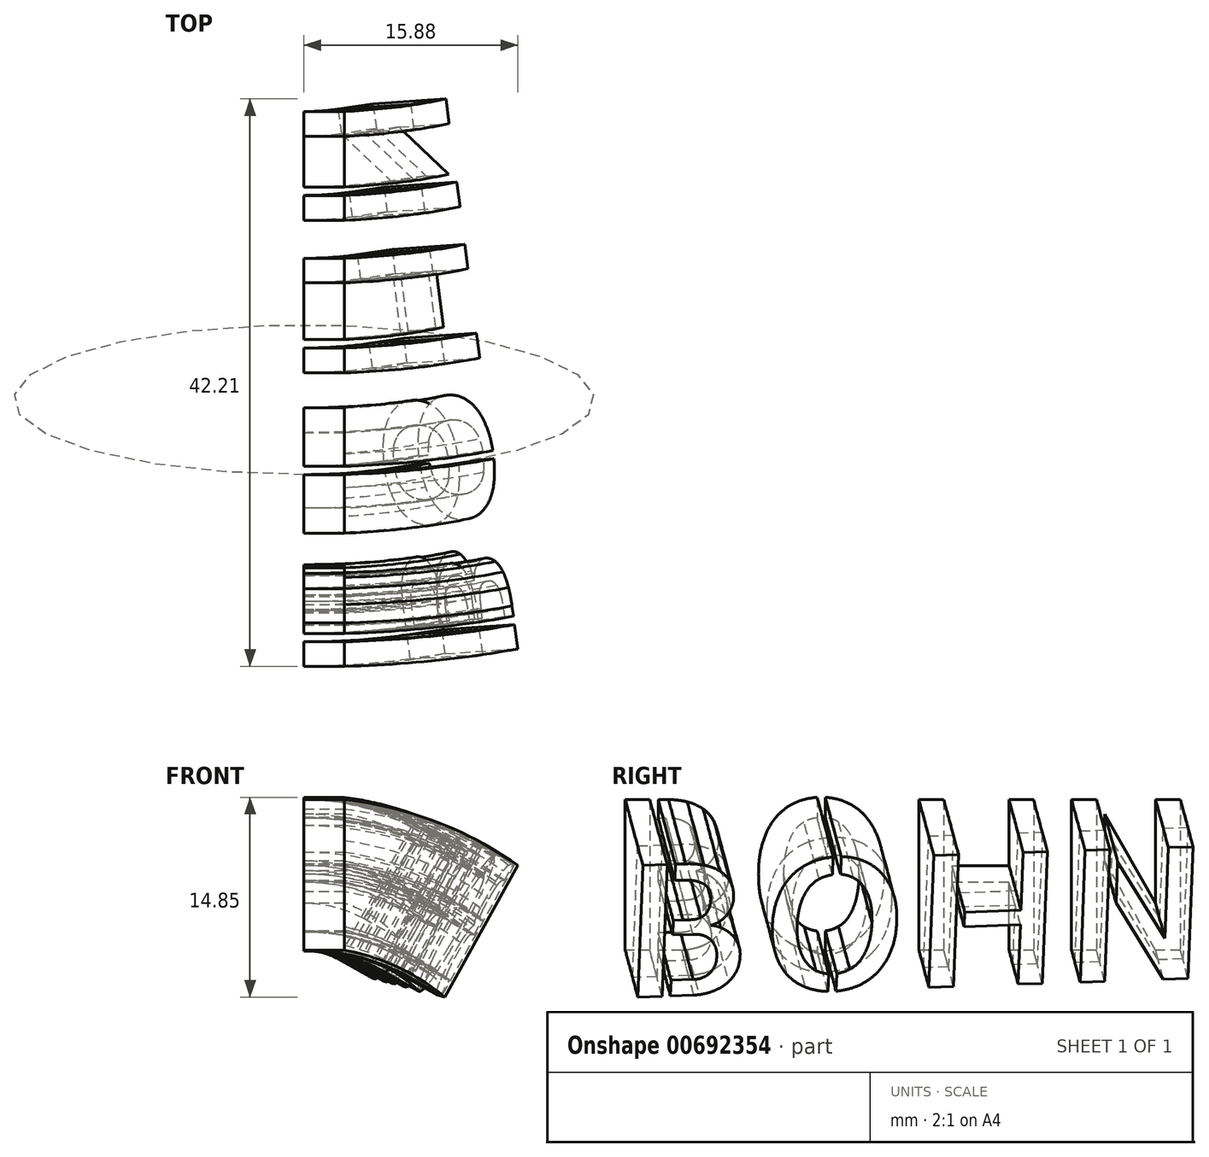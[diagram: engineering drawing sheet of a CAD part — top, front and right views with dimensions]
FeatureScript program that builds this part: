
annotation { "Feature Type Name" : "Feature", "Feature Type Description" : "" }
export const myFeature = defineFeature(function(context is Context, id is Id, definition is map)
    precondition{}
    {
        {
            var Q0;
            Q0=qCreatedBy(makeId("Right.planeOp"),FACE);
            var sketch = newSketch(context, id + "F0", { "sketchPlane" : qUnion([Q0])});
            skText(sketch, "E0", { "text": "BOHN", "fontName": "AllertaStencil-Regular.ttf"});
            const initialGuessF0  = {"E0": [-0.01671, 0.0177, 1, 0, 0.0112]};
            skSetInitialGuess(sketch, initialGuessF0);
            skSolve(sketch);
        }
        {
            var Q0;
            Q0=makeQuery(id+"F0.imprint","IMPRINT",FACE,{"disambiguationData":[TD([[makeQuery(id+"F0.imprint","IMPRINT",EDGE,{"derivedFrom":sQuery(id+"F0.wireOp",EDGE,"E0.sketch_text.stroke-79")}),-1.0]])]});
            var sketch = newSketch(context, id + "F1", { "sketchPlane" : qUnion([Q0])});
            skPoint(sketch, "E1", {"position": v(-30.52, 17.7) * mm});
            skPoint(sketch, "E2", {"position": v(-30.52, 31.5) * mm});
            skPoint(sketch, "E3", {"position": v(-22.23, 5.05) * mm});
            skSolve(sketch);
        }
        {
            var Q0;
            Q0 = qSketchRegion(id + "F0", true);
            extrude(context, id + "F2", {"entities" : qUnion([Q0]), "depth" : 3 * mm, "offsetDistance" : 25 * mm});
        }
        {
            var Q0;
            Q0=qCreatedBy(makeId("Right.planeOp"),FACE);
            var sketch = newSketch(context, id + "F3", { "sketchPlane" : qUnion([Q0])});
            skLineSegment(sketch, "E4", {"start": v(-30.76, -2.74) * mm, "end": v(47.8, 18.27) * mm, "construction": true});
            skSolve(sketch);
        }
        {
            var Q0;
            Q0=makeQuery(id+"F2.opExtrude","SWEPT_FACE",FACE,{"disambiguationData":[OSD([sQuery(id+"F0.wireOp",EDGE,"E0.sketch_text.stroke-17")])]});
            var Q1;
            Q1=makeQuery(id+"F2.opExtrude","SWEPT_FACE",FACE,{"disambiguationData":[OSD([sQuery(id+"F0.wireOp",EDGE,"E0.sketch_text.stroke-28")])]});
            var Q2;
            Q2=makeQuery(id+"F2.opExtrude","SWEPT_FACE",FACE,{"disambiguationData":[OSD([sQuery(id+"F0.wireOp",EDGE,"E0.sketch_text.stroke-29")])]});
            var Q3;
            Q3=makeQuery(id+"F2.opExtrude","SWEPT_FACE",FACE,{"disambiguationData":[OSD([sQuery(id+"F0.wireOp",EDGE,"E0.sketch_text.stroke-10")])]});
            var Q4;
            Q4=makeQuery(id+"F2.opExtrude","CAP_FACE",FACE,{"disambiguationData":[OSD([sQuery(id+"F0.wireOp",EDGE,"E0.sketch_text.stroke-0"),sQuery(id+"F0.wireOp",EDGE,"E0.sketch_text.stroke-1"),sQuery(id+"F0.wireOp",EDGE,"E0.sketch_text.stroke-2"),sQuery(id+"F0.wireOp",EDGE,"E0.sketch_text.stroke-3"),sQuery(id+"F0.wireOp",EDGE,"E0.sketch_text.stroke-4"),sQuery(id+"F0.wireOp",EDGE,"E0.sketch_text.stroke-5"),sQuery(id+"F0.wireOp",EDGE,"E0.sketch_text.stroke-6"),sQuery(id+"F0.wireOp",EDGE,"E0.sketch_text.stroke-7"),sQuery(id+"F0.wireOp",EDGE,"E0.sketch_text.stroke-8"),sQuery(id+"F0.wireOp",EDGE,"E0.sketch_text.stroke-9"),sQuery(id+"F0.wireOp",EDGE,"E0.sketch_text.stroke-10"),sQuery(id+"F0.wireOp",EDGE,"E0.sketch_text.stroke-11"),sQuery(id+"F0.wireOp",EDGE,"E0.sketch_text.stroke-12"),sQuery(id+"F0.wireOp",EDGE,"E0.sketch_text.stroke-13"),sQuery(id+"F0.wireOp",EDGE,"E0.sketch_text.stroke-14"),sQuery(id+"F0.wireOp",EDGE,"E0.sketch_text.stroke-15"),sQuery(id+"F0.wireOp",EDGE,"E0.sketch_text.stroke-16"),sQuery(id+"F0.wireOp",EDGE,"E0.sketch_text.stroke-17"),sQuery(id+"F0.wireOp",EDGE,"E0.sketch_text.stroke-18"),sQuery(id+"F0.wireOp",EDGE,"E0.sketch_text.stroke-19"),sQuery(id+"F0.wireOp",EDGE,"E0.sketch_text.stroke-20"),sQuery(id+"F0.wireOp",EDGE,"E0.sketch_text.stroke-21"),sQuery(id+"F0.wireOp",EDGE,"E0.sketch_text.stroke-22"),sQuery(id+"F0.wireOp",EDGE,"E0.sketch_text.stroke-23"),sQuery(id+"F0.wireOp",EDGE,"E0.sketch_text.stroke-24"),sQuery(id+"F0.wireOp",EDGE,"E0.sketch_text.stroke-25"),sQuery(id+"F0.wireOp",EDGE,"E0.sketch_text.stroke-26"),sQuery(id+"F0.wireOp",EDGE,"E0.sketch_text.stroke-27"),sQuery(id+"F0.wireOp",EDGE,"E0.sketch_text.stroke-28"),sQuery(id+"F0.wireOp",EDGE,"E0.sketch_text.stroke-29"),sQuery(id+"F0.wireOp",EDGE,"E0.sketch_text.stroke-30"),sQuery(id+"F0.wireOp",EDGE,"E0.sketch_text.stroke-31"),sQuery(id+"F0.wireOp",EDGE,"E0.sketch_text.stroke-32"),sQuery(id+"F0.wireOp",EDGE,"E0.sketch_text.stroke-33"),sQuery(id+"F0.wireOp",EDGE,"E0.sketch_text.stroke-34"),sQuery(id+"F0.wireOp",EDGE,"E0.sketch_text.stroke-35"),sQuery(id+"F0.wireOp",EDGE,"E0.sketch_text.stroke-36"),sQuery(id+"F0.wireOp",EDGE,"E0.sketch_text.stroke-37"),sQuery(id+"F0.wireOp",EDGE,"E0.sketch_text.stroke-38")])],"isStart":false});
            var Q5;
            Q5=makeQuery(id+"F2.opExtrude","SWEPT_FACE",FACE,{"disambiguationData":[OSD([sQuery(id+"F0.wireOp",EDGE,"E0.sketch_text.stroke-12")])]});
            var Q6;
            Q6=makeQuery(id+"F2.opExtrude","SWEPT_FACE",FACE,{"disambiguationData":[OSD([sQuery(id+"F0.wireOp",EDGE,"E0.sketch_text.stroke-11")])]});
            var Q7;
            Q7=makeQuery(id+"F2.opExtrude","SWEPT_FACE",FACE,{"disambiguationData":[OSD([sQuery(id+"F0.wireOp",EDGE,"E0.sketch_text.stroke-41")])]});
            var Q8;
            Q8=makeQuery(id+"F2.opExtrude","SWEPT_FACE",FACE,{"disambiguationData":[OSD([sQuery(id+"F0.wireOp",EDGE,"E0.sketch_text.stroke-42")])]});
            var Q9;
            Q9=makeQuery(id+"F2.opExtrude","SWEPT_FACE",FACE,{"disambiguationData":[OSD([sQuery(id+"F0.wireOp",EDGE,"E0.sketch_text.stroke-39")])]});
            var Q10;
            Q10=makeQuery(id+"F2.opExtrude","CAP_FACE",FACE,{"disambiguationData":[OSD([sQuery(id+"F0.wireOp",EDGE,"E0.sketch_text.stroke-39"),sQuery(id+"F0.wireOp",EDGE,"E0.sketch_text.stroke-40"),sQuery(id+"F0.wireOp",EDGE,"E0.sketch_text.stroke-41"),sQuery(id+"F0.wireOp",EDGE,"E0.sketch_text.stroke-42")])],"isStart":false});
            var Q11;
            Q11=makeQuery(id+"F2.opExtrude","SWEPT_FACE",FACE,{"disambiguationData":[OSD([sQuery(id+"F0.wireOp",EDGE,"E0.sketch_text.stroke-56")])]});
            var Q12;
            Q12=makeQuery(id+"F2.opExtrude","CAP_FACE",FACE,{"disambiguationData":[OSD([sQuery(id+"F0.wireOp",EDGE,"E0.sketch_text.stroke-43"),sQuery(id+"F0.wireOp",EDGE,"E0.sketch_text.stroke-44"),sQuery(id+"F0.wireOp",EDGE,"E0.sketch_text.stroke-45"),sQuery(id+"F0.wireOp",EDGE,"E0.sketch_text.stroke-46"),sQuery(id+"F0.wireOp",EDGE,"E0.sketch_text.stroke-47"),sQuery(id+"F0.wireOp",EDGE,"E0.sketch_text.stroke-48"),sQuery(id+"F0.wireOp",EDGE,"E0.sketch_text.stroke-49"),sQuery(id+"F0.wireOp",EDGE,"E0.sketch_text.stroke-50"),sQuery(id+"F0.wireOp",EDGE,"E0.sketch_text.stroke-51"),sQuery(id+"F0.wireOp",EDGE,"E0.sketch_text.stroke-52"),sQuery(id+"F0.wireOp",EDGE,"E0.sketch_text.stroke-53"),sQuery(id+"F0.wireOp",EDGE,"E0.sketch_text.stroke-54"),sQuery(id+"F0.wireOp",EDGE,"E0.sketch_text.stroke-55"),sQuery(id+"F0.wireOp",EDGE,"E0.sketch_text.stroke-56"),sQuery(id+"F0.wireOp",EDGE,"E0.sketch_text.stroke-57"),sQuery(id+"F0.wireOp",EDGE,"E0.sketch_text.stroke-58"),sQuery(id+"F0.wireOp",EDGE,"E0.sketch_text.stroke-59"),sQuery(id+"F0.wireOp",EDGE,"E0.sketch_text.stroke-60")])],"isStart":false});
            var Q13;
            Q13=makeQuery(id+"F2.opExtrude","SWEPT_FACE",FACE,{"disambiguationData":[OSD([sQuery(id+"F0.wireOp",EDGE,"E0.sketch_text.stroke-69")])]});
            var Q14;
            Q14=makeQuery(id+"F2.opExtrude","CAP_FACE",FACE,{"disambiguationData":[OSD([sQuery(id+"F0.wireOp",EDGE,"E0.sketch_text.stroke-61"),sQuery(id+"F0.wireOp",EDGE,"E0.sketch_text.stroke-62"),sQuery(id+"F0.wireOp",EDGE,"E0.sketch_text.stroke-63"),sQuery(id+"F0.wireOp",EDGE,"E0.sketch_text.stroke-64"),sQuery(id+"F0.wireOp",EDGE,"E0.sketch_text.stroke-65"),sQuery(id+"F0.wireOp",EDGE,"E0.sketch_text.stroke-66"),sQuery(id+"F0.wireOp",EDGE,"E0.sketch_text.stroke-67"),sQuery(id+"F0.wireOp",EDGE,"E0.sketch_text.stroke-68"),sQuery(id+"F0.wireOp",EDGE,"E0.sketch_text.stroke-69"),sQuery(id+"F0.wireOp",EDGE,"E0.sketch_text.stroke-70"),sQuery(id+"F0.wireOp",EDGE,"E0.sketch_text.stroke-71"),sQuery(id+"F0.wireOp",EDGE,"E0.sketch_text.stroke-72"),sQuery(id+"F0.wireOp",EDGE,"E0.sketch_text.stroke-73"),sQuery(id+"F0.wireOp",EDGE,"E0.sketch_text.stroke-74"),sQuery(id+"F0.wireOp",EDGE,"E0.sketch_text.stroke-75"),sQuery(id+"F0.wireOp",EDGE,"E0.sketch_text.stroke-76"),sQuery(id+"F0.wireOp",EDGE,"E0.sketch_text.stroke-77"),sQuery(id+"F0.wireOp",EDGE,"E0.sketch_text.stroke-78")])],"isStart":false});
            var Q15;
            Q15=makeQuery(id+"F2.opExtrude","SWEPT_FACE",FACE,{"disambiguationData":[OSD([sQuery(id+"F0.wireOp",EDGE,"E0.sketch_text.stroke-78")])]});
            var Q16;
            Q16=makeQuery(id+"F2.opExtrude","SWEPT_FACE",FACE,{"disambiguationData":[OSD([sQuery(id+"F0.wireOp",EDGE,"E0.sketch_text.stroke-85")])]});
            var Q17;
            Q17=makeQuery(id+"F2.opExtrude","SWEPT_FACE",FACE,{"disambiguationData":[OSD([sQuery(id+"F0.wireOp",EDGE,"E0.sketch_text.stroke-83")])]});
            var Q18;
            Q18=makeQuery(id+"F2.opExtrude","SWEPT_FACE",FACE,{"disambiguationData":[OSD([sQuery(id+"F0.wireOp",EDGE,"E0.sketch_text.stroke-84")])]});
            var Q19;
            Q19=makeQuery(id+"F2.opExtrude","SWEPT_FACE",FACE,{"disambiguationData":[OSD([sQuery(id+"F0.wireOp",EDGE,"E0.sketch_text.stroke-86")])]});
            var Q20;
            Q20=makeQuery(id+"F2.opExtrude","SWEPT_FACE",FACE,{"disambiguationData":[OSD([sQuery(id+"F0.wireOp",EDGE,"E0.sketch_text.stroke-79")])]});
            var Q21;
            Q21=makeQuery(id+"F2.opExtrude","CAP_FACE",FACE,{"disambiguationData":[OSD([sQuery(id+"F0.wireOp",EDGE,"E0.sketch_text.stroke-79"),sQuery(id+"F0.wireOp",EDGE,"E0.sketch_text.stroke-80"),sQuery(id+"F0.wireOp",EDGE,"E0.sketch_text.stroke-81"),sQuery(id+"F0.wireOp",EDGE,"E0.sketch_text.stroke-82"),sQuery(id+"F0.wireOp",EDGE,"E0.sketch_text.stroke-83"),sQuery(id+"F0.wireOp",EDGE,"E0.sketch_text.stroke-84"),sQuery(id+"F0.wireOp",EDGE,"E0.sketch_text.stroke-85"),sQuery(id+"F0.wireOp",EDGE,"E0.sketch_text.stroke-86")])],"isStart":false});
            var Q22;
            Q22=makeQuery(id+"F2.opExtrude","SWEPT_FACE",FACE,{"disambiguationData":[OSD([sQuery(id+"F0.wireOp",EDGE,"E0.sketch_text.stroke-82")])]});
            var Q23;
            Q23=makeQuery(id+"F2.opExtrude","SWEPT_FACE",FACE,{"disambiguationData":[OSD([sQuery(id+"F0.wireOp",EDGE,"E0.sketch_text.stroke-87")])]});
            var Q24;
            Q24=makeQuery(id+"F2.opExtrude","CAP_FACE",FACE,{"disambiguationData":[OSD([sQuery(id+"F0.wireOp",EDGE,"E0.sketch_text.stroke-87"),sQuery(id+"F0.wireOp",EDGE,"E0.sketch_text.stroke-88"),sQuery(id+"F0.wireOp",EDGE,"E0.sketch_text.stroke-89"),sQuery(id+"F0.wireOp",EDGE,"E0.sketch_text.stroke-90")])],"isStart":false});
            var Q25;
            Q25=makeQuery(id+"F2.opExtrude","SWEPT_FACE",FACE,{"disambiguationData":[OSD([sQuery(id+"F0.wireOp",EDGE,"E0.sketch_text.stroke-89")])]});
            var Q26;
            Q26=makeQuery(id+"F2.opExtrude","SWEPT_FACE",FACE,{"disambiguationData":[OSD([sQuery(id+"F0.wireOp",EDGE,"E0.sketch_text.stroke-90")])]});
            var Q27;
            Q27=makeQuery(id+"F2.opExtrude","SWEPT_FACE",FACE,{"disambiguationData":[OSD([sQuery(id+"F0.wireOp",EDGE,"E0.sketch_text.stroke-97")])]});
            var Q28;
            Q28=makeQuery(id+"F2.opExtrude","SWEPT_FACE",FACE,{"disambiguationData":[OSD([sQuery(id+"F0.wireOp",EDGE,"E0.sketch_text.stroke-95")])]});
            var Q29;
            Q29=makeQuery(id+"F2.opExtrude","SWEPT_FACE",FACE,{"disambiguationData":[OSD([sQuery(id+"F0.wireOp",EDGE,"E0.sketch_text.stroke-96")])]});
            var Q30;
            Q30=makeQuery(id+"F2.opExtrude","SWEPT_FACE",FACE,{"disambiguationData":[OSD([sQuery(id+"F0.wireOp",EDGE,"E0.sketch_text.stroke-91")])]});
            var Q31;
            Q31=makeQuery(id+"F2.opExtrude","CAP_FACE",FACE,{"disambiguationData":[OSD([sQuery(id+"F0.wireOp",EDGE,"E0.sketch_text.stroke-91"),sQuery(id+"F0.wireOp",EDGE,"E0.sketch_text.stroke-92"),sQuery(id+"F0.wireOp",EDGE,"E0.sketch_text.stroke-93"),sQuery(id+"F0.wireOp",EDGE,"E0.sketch_text.stroke-94"),sQuery(id+"F0.wireOp",EDGE,"E0.sketch_text.stroke-95"),sQuery(id+"F0.wireOp",EDGE,"E0.sketch_text.stroke-96"),sQuery(id+"F0.wireOp",EDGE,"E0.sketch_text.stroke-97")])],"isStart":false});
            var Q32;
            Q32=makeQuery(id+"F2.opExtrude","SWEPT_FACE",FACE,{"disambiguationData":[OSD([sQuery(id+"F0.wireOp",EDGE,"E0.sketch_text.stroke-92")])]});
            var Q33;
            Q33=makeQuery(id+"F2.opExtrude","SWEPT_FACE",FACE,{"disambiguationData":[OSD([sQuery(id+"F0.wireOp",EDGE,"E0.sketch_text.stroke-93")])]});
            var Q34;
            Q34=makeQuery(id+"F2.opExtrude","SWEPT_FACE",FACE,{"disambiguationData":[OSD([sQuery(id+"F0.wireOp",EDGE,"E0.sketch_text.stroke-98")])]});
            var Q35;
            Q35=makeQuery(id+"F2.opExtrude","CAP_FACE",FACE,{"disambiguationData":[OSD([sQuery(id+"F0.wireOp",EDGE,"E0.sketch_text.stroke-98"),sQuery(id+"F0.wireOp",EDGE,"E0.sketch_text.stroke-99"),sQuery(id+"F0.wireOp",EDGE,"E0.sketch_text.stroke-100"),sQuery(id+"F0.wireOp",EDGE,"E0.sketch_text.stroke-101")])],"isStart":false});
            var Q36;
            Q36=makeQuery(id+"F2.opExtrude","SWEPT_FACE",FACE,{"disambiguationData":[OSD([sQuery(id+"F0.wireOp",EDGE,"E0.sketch_text.stroke-100")])]});
            var Q37;
            Q37=makeQuery(id+"F1.imprint","IMPRINT",FACE,{"disambiguationData":[TD([[makeQuery(id+"F1.imprint","IMPRINT",EDGE,{"derivedFrom":makeQuery(id+"F0.imprint","IMPRINT",EDGE,{"derivedFrom":sQuery(id+"F0.wireOp",EDGE,"E0.sketch_text.stroke-79")})}),-1.0]])]});
            var Q38;
            Q38=makeQuery(id+"F2.opExtrude","SWEPT_FACE",FACE,{"disambiguationData":[OSD([sQuery(id+"F0.wireOp",EDGE,"E0.sketch_text.stroke-30")])]});
            var Q39;
            Q39=makeQuery(id+"F2.opExtrude","SWEPT_FACE",FACE,{"disambiguationData":[OSD([sQuery(id+"F0.wireOp",EDGE,"E0.sketch_text.stroke-18")])]});
            var Q40;
            Q40=makeQuery(id+"F2.opExtrude","CAP_FACE",FACE,{"disambiguationData":[OSD([sQuery(id+"F0.wireOp",EDGE,"E0.sketch_text.stroke-0"),sQuery(id+"F0.wireOp",EDGE,"E0.sketch_text.stroke-1"),sQuery(id+"F0.wireOp",EDGE,"E0.sketch_text.stroke-2"),sQuery(id+"F0.wireOp",EDGE,"E0.sketch_text.stroke-3"),sQuery(id+"F0.wireOp",EDGE,"E0.sketch_text.stroke-4"),sQuery(id+"F0.wireOp",EDGE,"E0.sketch_text.stroke-5"),sQuery(id+"F0.wireOp",EDGE,"E0.sketch_text.stroke-6"),sQuery(id+"F0.wireOp",EDGE,"E0.sketch_text.stroke-7"),sQuery(id+"F0.wireOp",EDGE,"E0.sketch_text.stroke-8"),sQuery(id+"F0.wireOp",EDGE,"E0.sketch_text.stroke-9"),sQuery(id+"F0.wireOp",EDGE,"E0.sketch_text.stroke-10"),sQuery(id+"F0.wireOp",EDGE,"E0.sketch_text.stroke-11"),sQuery(id+"F0.wireOp",EDGE,"E0.sketch_text.stroke-12"),sQuery(id+"F0.wireOp",EDGE,"E0.sketch_text.stroke-13"),sQuery(id+"F0.wireOp",EDGE,"E0.sketch_text.stroke-14"),sQuery(id+"F0.wireOp",EDGE,"E0.sketch_text.stroke-15"),sQuery(id+"F0.wireOp",EDGE,"E0.sketch_text.stroke-16"),sQuery(id+"F0.wireOp",EDGE,"E0.sketch_text.stroke-17"),sQuery(id+"F0.wireOp",EDGE,"E0.sketch_text.stroke-18"),sQuery(id+"F0.wireOp",EDGE,"E0.sketch_text.stroke-19"),sQuery(id+"F0.wireOp",EDGE,"E0.sketch_text.stroke-20"),sQuery(id+"F0.wireOp",EDGE,"E0.sketch_text.stroke-21"),sQuery(id+"F0.wireOp",EDGE,"E0.sketch_text.stroke-22"),sQuery(id+"F0.wireOp",EDGE,"E0.sketch_text.stroke-23"),sQuery(id+"F0.wireOp",EDGE,"E0.sketch_text.stroke-24"),sQuery(id+"F0.wireOp",EDGE,"E0.sketch_text.stroke-25"),sQuery(id+"F0.wireOp",EDGE,"E0.sketch_text.stroke-26"),sQuery(id+"F0.wireOp",EDGE,"E0.sketch_text.stroke-27"),sQuery(id+"F0.wireOp",EDGE,"E0.sketch_text.stroke-28"),sQuery(id+"F0.wireOp",EDGE,"E0.sketch_text.stroke-29"),sQuery(id+"F0.wireOp",EDGE,"E0.sketch_text.stroke-30"),sQuery(id+"F0.wireOp",EDGE,"E0.sketch_text.stroke-31"),sQuery(id+"F0.wireOp",EDGE,"E0.sketch_text.stroke-32"),sQuery(id+"F0.wireOp",EDGE,"E0.sketch_text.stroke-33"),sQuery(id+"F0.wireOp",EDGE,"E0.sketch_text.stroke-34"),sQuery(id+"F0.wireOp",EDGE,"E0.sketch_text.stroke-35"),sQuery(id+"F0.wireOp",EDGE,"E0.sketch_text.stroke-36"),sQuery(id+"F0.wireOp",EDGE,"E0.sketch_text.stroke-37"),sQuery(id+"F0.wireOp",EDGE,"E0.sketch_text.stroke-38")])],"isStart":true});
            var Q41;
            Q41=makeQuery(id+"F2.opExtrude","SWEPT_FACE",FACE,{"disambiguationData":[OSD([sQuery(id+"F0.wireOp",EDGE,"E0.sketch_text.stroke-19")])]});
            var Q42;
            Q42=makeQuery(id+"F2.opExtrude","CAP_FACE",FACE,{"disambiguationData":[OSD([sQuery(id+"F0.wireOp",EDGE,"E0.sketch_text.stroke-39"),sQuery(id+"F0.wireOp",EDGE,"E0.sketch_text.stroke-40"),sQuery(id+"F0.wireOp",EDGE,"E0.sketch_text.stroke-41"),sQuery(id+"F0.wireOp",EDGE,"E0.sketch_text.stroke-42")])],"isStart":true});
            var Q43;
            Q43=makeQuery(id+"F2.opExtrude","SWEPT_FACE",FACE,{"disambiguationData":[OSD([sQuery(id+"F0.wireOp",EDGE,"E0.sketch_text.stroke-40")])]});
            var Q44;
            Q44=makeQuery(id+"F2.opExtrude","CAP_FACE",FACE,{"disambiguationData":[OSD([sQuery(id+"F0.wireOp",EDGE,"E0.sketch_text.stroke-43"),sQuery(id+"F0.wireOp",EDGE,"E0.sketch_text.stroke-44"),sQuery(id+"F0.wireOp",EDGE,"E0.sketch_text.stroke-45"),sQuery(id+"F0.wireOp",EDGE,"E0.sketch_text.stroke-46"),sQuery(id+"F0.wireOp",EDGE,"E0.sketch_text.stroke-47"),sQuery(id+"F0.wireOp",EDGE,"E0.sketch_text.stroke-48"),sQuery(id+"F0.wireOp",EDGE,"E0.sketch_text.stroke-49"),sQuery(id+"F0.wireOp",EDGE,"E0.sketch_text.stroke-50"),sQuery(id+"F0.wireOp",EDGE,"E0.sketch_text.stroke-51"),sQuery(id+"F0.wireOp",EDGE,"E0.sketch_text.stroke-52"),sQuery(id+"F0.wireOp",EDGE,"E0.sketch_text.stroke-53"),sQuery(id+"F0.wireOp",EDGE,"E0.sketch_text.stroke-54"),sQuery(id+"F0.wireOp",EDGE,"E0.sketch_text.stroke-55"),sQuery(id+"F0.wireOp",EDGE,"E0.sketch_text.stroke-56"),sQuery(id+"F0.wireOp",EDGE,"E0.sketch_text.stroke-57"),sQuery(id+"F0.wireOp",EDGE,"E0.sketch_text.stroke-58"),sQuery(id+"F0.wireOp",EDGE,"E0.sketch_text.stroke-59"),sQuery(id+"F0.wireOp",EDGE,"E0.sketch_text.stroke-60")])],"isStart":true});
            var Q45;
            Q45=makeQuery(id+"F2.opExtrude","SWEPT_FACE",FACE,{"disambiguationData":[OSD([sQuery(id+"F0.wireOp",EDGE,"E0.sketch_text.stroke-47")])]});
            var Q46;
            Q46=makeQuery(id+"F2.opExtrude","CAP_FACE",FACE,{"disambiguationData":[OSD([sQuery(id+"F0.wireOp",EDGE,"E0.sketch_text.stroke-61"),sQuery(id+"F0.wireOp",EDGE,"E0.sketch_text.stroke-62"),sQuery(id+"F0.wireOp",EDGE,"E0.sketch_text.stroke-63"),sQuery(id+"F0.wireOp",EDGE,"E0.sketch_text.stroke-64"),sQuery(id+"F0.wireOp",EDGE,"E0.sketch_text.stroke-65"),sQuery(id+"F0.wireOp",EDGE,"E0.sketch_text.stroke-66"),sQuery(id+"F0.wireOp",EDGE,"E0.sketch_text.stroke-67"),sQuery(id+"F0.wireOp",EDGE,"E0.sketch_text.stroke-68"),sQuery(id+"F0.wireOp",EDGE,"E0.sketch_text.stroke-69"),sQuery(id+"F0.wireOp",EDGE,"E0.sketch_text.stroke-70"),sQuery(id+"F0.wireOp",EDGE,"E0.sketch_text.stroke-71"),sQuery(id+"F0.wireOp",EDGE,"E0.sketch_text.stroke-72"),sQuery(id+"F0.wireOp",EDGE,"E0.sketch_text.stroke-73"),sQuery(id+"F0.wireOp",EDGE,"E0.sketch_text.stroke-74"),sQuery(id+"F0.wireOp",EDGE,"E0.sketch_text.stroke-75"),sQuery(id+"F0.wireOp",EDGE,"E0.sketch_text.stroke-76"),sQuery(id+"F0.wireOp",EDGE,"E0.sketch_text.stroke-77"),sQuery(id+"F0.wireOp",EDGE,"E0.sketch_text.stroke-78")])],"isStart":true});
            var Q47;
            Q47=makeQuery(id+"F2.opExtrude","CAP_FACE",FACE,{"disambiguationData":[OSD([sQuery(id+"F0.wireOp",EDGE,"E0.sketch_text.stroke-79"),sQuery(id+"F0.wireOp",EDGE,"E0.sketch_text.stroke-80"),sQuery(id+"F0.wireOp",EDGE,"E0.sketch_text.stroke-81"),sQuery(id+"F0.wireOp",EDGE,"E0.sketch_text.stroke-82"),sQuery(id+"F0.wireOp",EDGE,"E0.sketch_text.stroke-83"),sQuery(id+"F0.wireOp",EDGE,"E0.sketch_text.stroke-84"),sQuery(id+"F0.wireOp",EDGE,"E0.sketch_text.stroke-85"),sQuery(id+"F0.wireOp",EDGE,"E0.sketch_text.stroke-86")])],"isStart":true});
            var Q48;
            Q48=makeQuery(id+"F2.opExtrude","SWEPT_FACE",FACE,{"disambiguationData":[OSD([sQuery(id+"F0.wireOp",EDGE,"E0.sketch_text.stroke-80")])]});
            var Q49;
            Q49=makeQuery(id+"F2.opExtrude","SWEPT_FACE",FACE,{"disambiguationData":[OSD([sQuery(id+"F0.wireOp",EDGE,"E0.sketch_text.stroke-81")])]});
            var Q50;
            Q50=makeQuery(id+"F2.opExtrude","CAP_FACE",FACE,{"disambiguationData":[OSD([sQuery(id+"F0.wireOp",EDGE,"E0.sketch_text.stroke-87"),sQuery(id+"F0.wireOp",EDGE,"E0.sketch_text.stroke-88"),sQuery(id+"F0.wireOp",EDGE,"E0.sketch_text.stroke-89"),sQuery(id+"F0.wireOp",EDGE,"E0.sketch_text.stroke-90")])],"isStart":true});
            var Q51;
            Q51=makeQuery(id+"F2.opExtrude","SWEPT_FACE",FACE,{"disambiguationData":[OSD([sQuery(id+"F0.wireOp",EDGE,"E0.sketch_text.stroke-88")])]});
            var Q52;
            Q52=makeQuery(id+"F2.opExtrude","CAP_FACE",FACE,{"disambiguationData":[OSD([sQuery(id+"F0.wireOp",EDGE,"E0.sketch_text.stroke-91"),sQuery(id+"F0.wireOp",EDGE,"E0.sketch_text.stroke-92"),sQuery(id+"F0.wireOp",EDGE,"E0.sketch_text.stroke-93"),sQuery(id+"F0.wireOp",EDGE,"E0.sketch_text.stroke-94"),sQuery(id+"F0.wireOp",EDGE,"E0.sketch_text.stroke-95"),sQuery(id+"F0.wireOp",EDGE,"E0.sketch_text.stroke-96"),sQuery(id+"F0.wireOp",EDGE,"E0.sketch_text.stroke-97")])],"isStart":true});
            var Q53;
            Q53=makeQuery(id+"F2.opExtrude","SWEPT_FACE",FACE,{"disambiguationData":[OSD([sQuery(id+"F0.wireOp",EDGE,"E0.sketch_text.stroke-94")])]});
            var Q54;
            Q54=makeQuery(id+"F2.opExtrude","CAP_FACE",FACE,{"disambiguationData":[OSD([sQuery(id+"F0.wireOp",EDGE,"E0.sketch_text.stroke-98"),sQuery(id+"F0.wireOp",EDGE,"E0.sketch_text.stroke-99"),sQuery(id+"F0.wireOp",EDGE,"E0.sketch_text.stroke-100"),sQuery(id+"F0.wireOp",EDGE,"E0.sketch_text.stroke-101")])],"isStart":true});
            var Q55;
            Q55=makeQuery(id+"F2.opExtrude","SWEPT_FACE",FACE,{"disambiguationData":[OSD([sQuery(id+"F0.wireOp",EDGE,"E0.sketch_text.stroke-99")])]});
            var Q56;
            Q56=makeQuery(id+"F2.opExtrude","SWEPT_FACE",FACE,{"disambiguationData":[OSD([sQuery(id+"F0.wireOp",EDGE,"E0.sketch_text.stroke-101")])]});
            var Q57;
            Q57=sQuery(id+"F3.wireOp",EDGE,"E4");
            revolve(context, id + "F4", {"entities" : qUnion([Q0, Q1, Q2, Q3, Q4, Q5, Q6, Q7, Q8, Q9, Q10, Q11, Q12, Q13, Q14, Q15, Q16, Q17, Q18, Q19, Q20, Q21, Q22, Q23, Q24, Q25, Q26, Q27, Q28, Q29, Q30, Q31, Q32, Q33, Q34, Q35, Q36, Q37, Q38, Q39, Q40, Q41, Q42, Q43, Q44, Q45, Q46, Q47, Q48, Q49, Q50, Q51, Q52, Q53, Q54, Q55, Q56]), "axis" : qUnion([Q57]), "revolveType" : RevolveType.ONE_DIRECTION, "angle" : 30 * degree});
        }
    });
